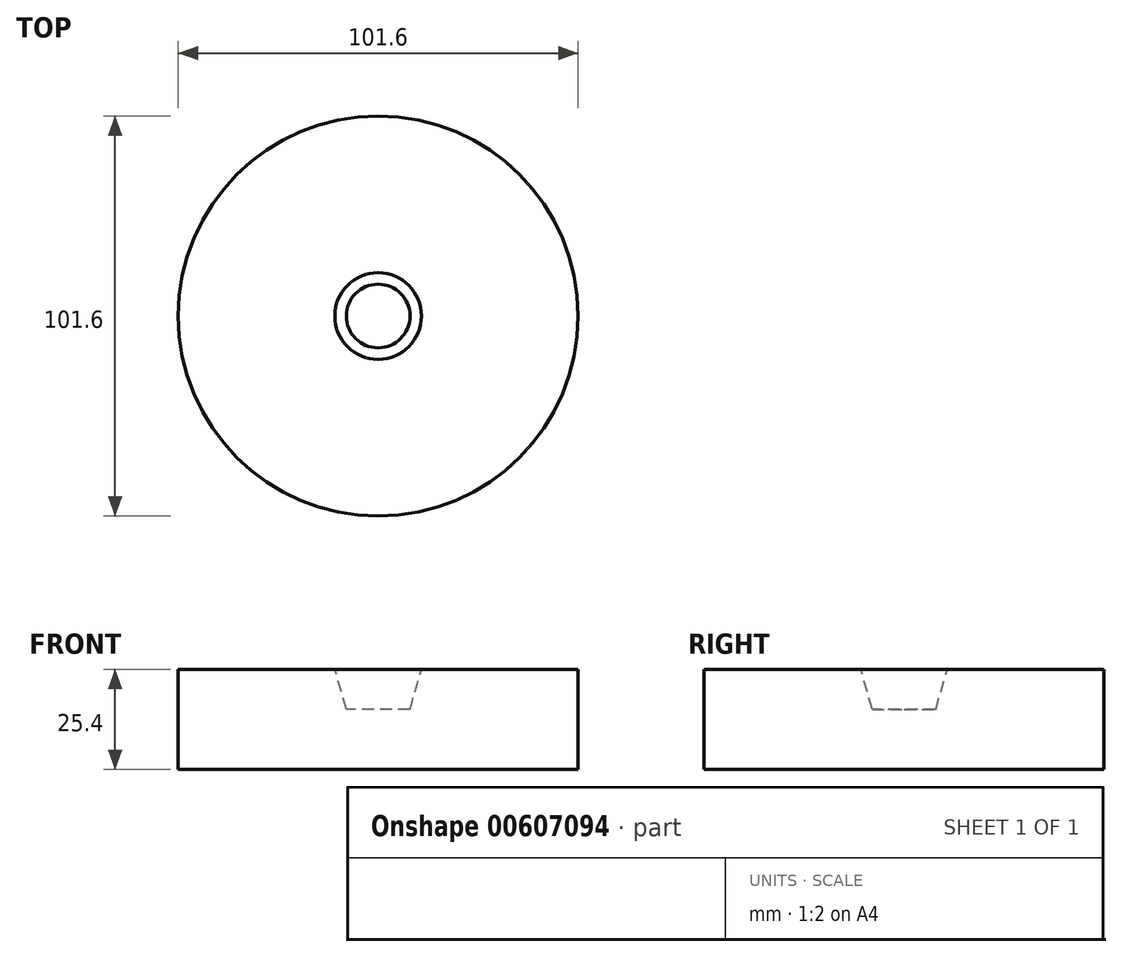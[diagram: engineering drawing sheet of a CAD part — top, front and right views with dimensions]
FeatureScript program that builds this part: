
annotation { "Feature Type Name" : "Feature", "Feature Type Description" : "" }
export const myFeature = defineFeature(function(context is Context, id is Id, definition is map)
    precondition{}
    {
        {
            var Q0;
            Q0=qCreatedBy(makeId("Top.planeOp"),FACE);
            var sketch = newSketch(context, id + "F0", { "sketchPlane" : qUnion([Q0])});
            skCircle(sketch, "E0", {"center": v(0, 0) * mm, "radius": 50.8 * mm});
            skSolve(sketch);
        }
        {
            var Q0;
            Q0 = qSketchRegion(id + "F0", true);
            extrude(context, id + "F1", {"entities" : qUnion([Q0]), "depth" : 25.4 * mm, "offsetDistance" : 25.4 * mm});
        }
        {
            var Q0;
            Q0=makeQuery(id+"F1.opExtrude","CAP_FACE",FACE,{"disambiguationData":[OSD([sQuery(id+"F0.wireOp",EDGE,"E0")])],"isStart":false});
            var sketch = newSketch(context, id + "F2", { "sketchPlane" : qUnion([Q0])});
            skCircle(sketch, "E1", {"center": v(0, 0) * mm, "radius": 11 * mm});
            skSolve(sketch);
        }
        {
            var Q0;
            Q0=makeQuery(id+"F2.imprint","IMPRINT",FACE,{"disambiguationData":[TD([[makeQuery(id+"F2.imprint","IMPRINT",EDGE,{"derivedFrom":sQuery(id+"F2.wireOp",EDGE,"E1")}),1.0]])]});
            extrude(context, id + "F3", {"entities" : qUnion([Q0]), "operationType" : NewBodyOperationType.REMOVE, "oppositeDirection" : true, "depth" : 10.16 * mm, "offsetDistance" : 25.4 * mm, "hasDraft" : true, "draftAngle" : 16 * degree, "draftPullDirection" : true});
        }
    });
